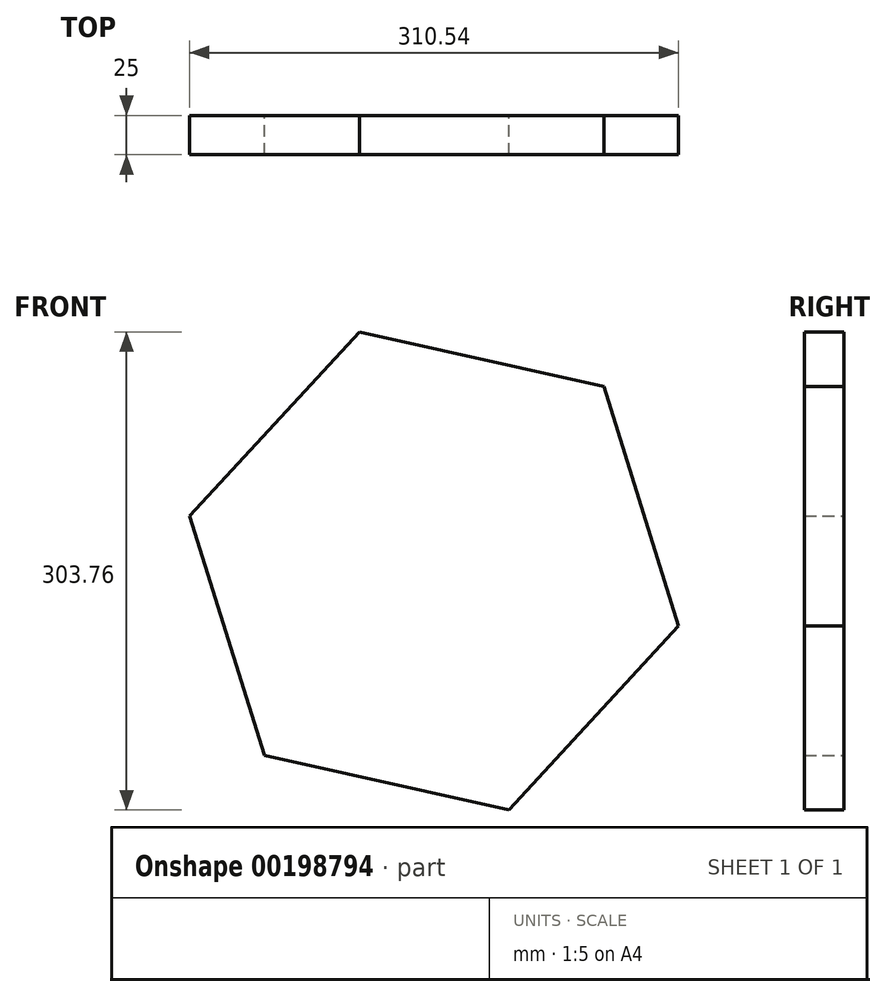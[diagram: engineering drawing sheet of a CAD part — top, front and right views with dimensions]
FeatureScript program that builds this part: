
annotation { "Feature Type Name" : "Feature", "Feature Type Description" : "" }
export const myFeature = defineFeature(function(context is Context, id is Id, definition is map)
    precondition{}
    {
        {
            var Q0;
            Q0=qCreatedBy(makeId("Front.planeOp"),FACE);
            var sketch = newSketch(context, id + "F0", { "sketchPlane" : qUnion([Q0])});
            skCircle(sketch, "E0.cCircle", {"center": v(0, 0) * mm, "radius": 137.8 * mm, "construction": true});
            skLineSegment(sketch, "E0.0", {"start": v(47.47, -151.88) * mm, "end": v(-107.8, -117.05) * mm});
            skLineSegment(sketch, "E0.1", {"start": v(-107.8, -117.05) * mm, "end": v(-155.27, 34.83) * mm});
            skLineSegment(sketch, "E0.2", {"start": v(-155.27, 34.83) * mm, "end": v(-47.47, 151.88) * mm});
            skLineSegment(sketch, "E0.3", {"start": v(-47.47, 151.88) * mm, "end": v(107.8, 117.05) * mm});
            skLineSegment(sketch, "E0.4", {"start": v(107.8, 117.05) * mm, "end": v(155.27, -34.83) * mm});
            skLineSegment(sketch, "E0.5", {"start": v(155.27, -34.83) * mm, "end": v(47.47, -151.88) * mm});
            skPoint(sketch, "E0.0.midPoint", {"position": v(-30.16, -134.47) * mm});
            skSolve(sketch);
        }
        {
            var Q0;
            Q0=makeQuery(id+"F0.imprint","IMPRINT",FACE,{"disambiguationData":[TD([[makeQuery(id+"F0.imprint","IMPRINT",EDGE,{"derivedFrom":sQuery(id+"F0.wireOp",EDGE,"E0.0")}),-1.0]])]});
            extrude(context, id + "F1", {"entities" : qUnion([Q0]), "depth" : 25 * mm});
        }
    });
